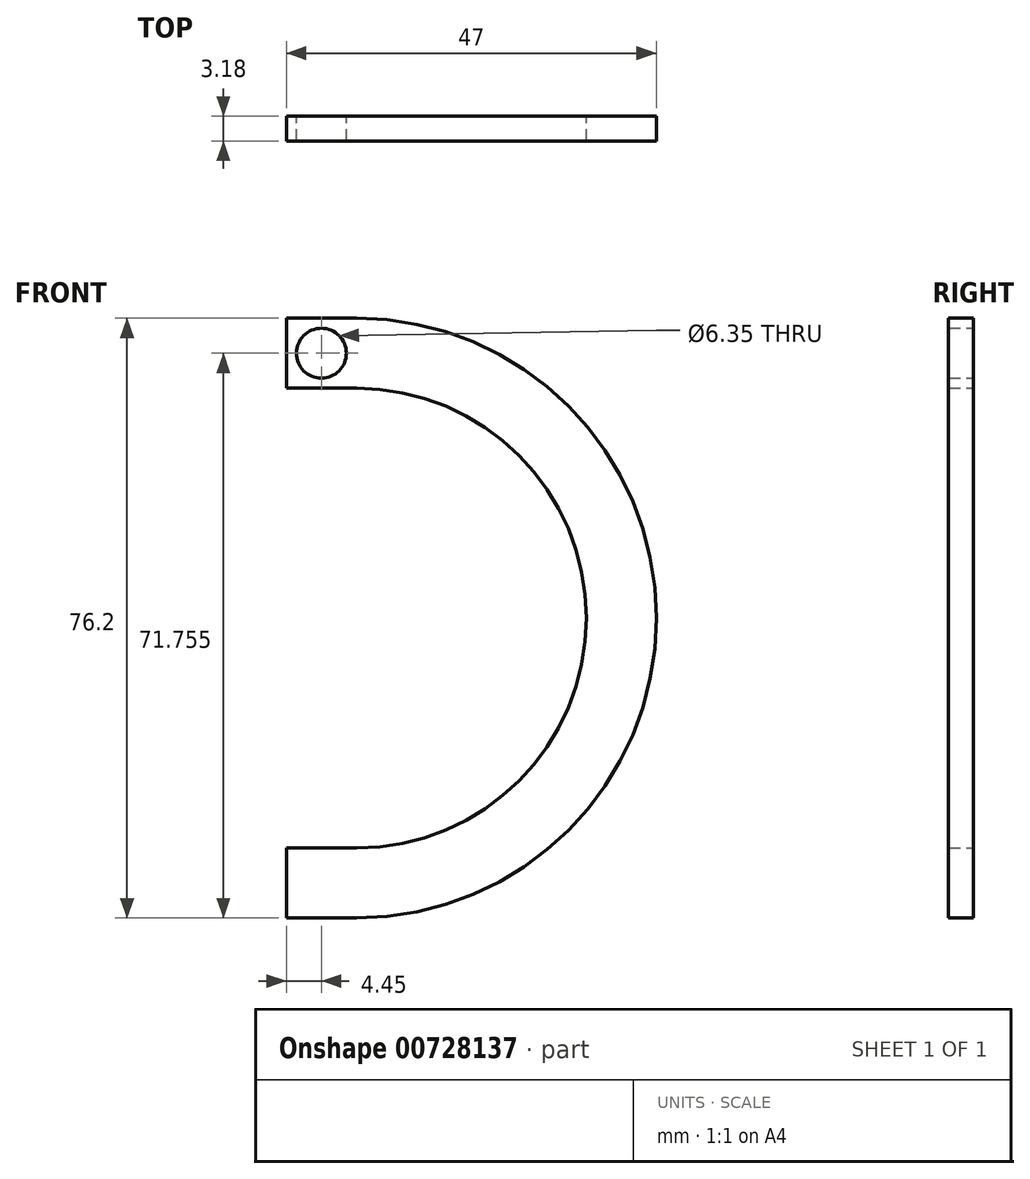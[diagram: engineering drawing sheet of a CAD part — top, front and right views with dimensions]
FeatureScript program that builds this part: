
annotation { "Feature Type Name" : "Feature", "Feature Type Description" : "" }
export const myFeature = defineFeature(function(context is Context, id is Id, definition is map)
    precondition{}
    {
        {
            var Q0;
            Q0=qCreatedBy(makeId("Front.planeOp"),FACE);
            var sketch = newSketch(context, id + "F0", { "sketchPlane" : qUnion([Q0])});
            skLineSegment(sketch, "E0.bottom", {"start": v(4.45, 38.1) * mm, "end": v(-4.44, 38.1) * mm});
            skLineSegment(sketch, "E0.top", {"start": v(4.44, -38.1) * mm, "end": v(-4.45, -38.1) * mm});
            skLineSegment(sketch, "E0.left", {"start": v(4.45, 38.1) * mm, "end": v(4.44, -38.1) * mm});
            skLineSegment(sketch, "E0.right", {"start": v(-4.44, 38.1) * mm, "end": v(-4.45, -38.1) * mm});
            skPoint(sketch, "E0.middle", {"position": v(0, 0) * mm});
            skArc(sketch, "E1", {"start": v(4.44, -38.1) * mm, "mid": v(42.55, 0) * mm, "end": v(4.45, 38.1) * mm});
            skArc(sketch, "E2", {"start": v(4.44, -29.2) * mm, "mid": v(33.65, 0) * mm, "end": v(4.45, 29.21) * mm});
            skLineSegment(sketch, "E3", {"start": v(4.45, 29.21) * mm, "end": v(-4.44, 29.21) * mm});
            skLineSegment(sketch, "E4", {"start": v(4.44, -29.2) * mm, "end": v(-4.45, -29.2) * mm});
            skCircle(sketch, "E5", {"center": v(0, 33.65) * mm, "radius": 3.18 * mm});
            skPoint(sketch, "E5.centerSnap0", {"position": v(0, 38.1) * mm});
            skSolve(sketch);
        }
        {
            var Q0;
            {var subQ0=sQuery(id+"F0.wireOp",EDGE,"E0.bottom");Q0=makeQuery(id+"F0.imprint","IMPRINT",FACE,{"disambiguationData":[TD([[makeQuery(id+"F0.imprint","IMPRINT",EDGE,{"derivedFrom":subQ0}),1.0]])]});}
            var Q1;
            {var subQ0=sQuery(id+"F0.wireOp",EDGE,"E0.top");Q1=makeQuery(id+"F0.imprint","IMPRINT",FACE,{"disambiguationData":[TD([[makeQuery(id+"F0.imprint","IMPRINT",EDGE,{"derivedFrom":subQ0}),-1.0]])]});}
            var Q2;
            {var subQ0=sQuery(id+"F0.wireOp",EDGE,"E1");Q2=makeQuery(id+"F0.imprint","IMPRINT",FACE,{"disambiguationData":[TD([[makeQuery(id+"F0.imprint","IMPRINT",EDGE,{"derivedFrom":subQ0}),1.0]])]});}
            extrude(context, id + "F1", {"entities" : qUnion([Q0, Q1, Q2]), "depth" : 3.17 * mm, "offsetDistance" : 25.4 * mm});
        }
    });
